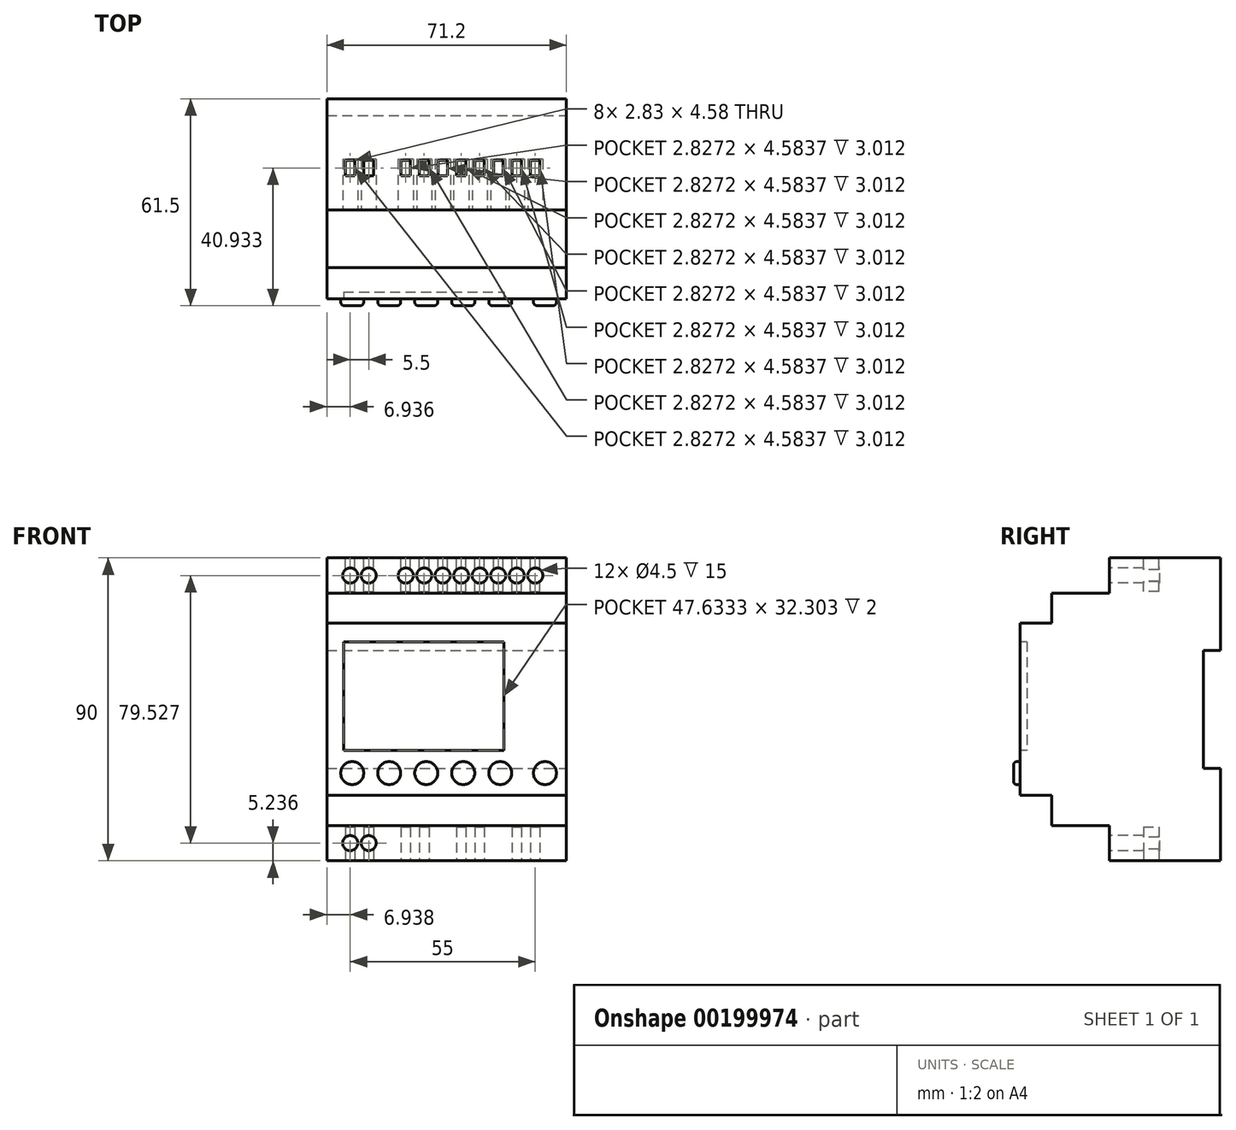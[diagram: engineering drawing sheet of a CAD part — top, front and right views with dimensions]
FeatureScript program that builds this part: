
annotation { "Feature Type Name" : "Feature", "Feature Type Description" : "" }
export const myFeature = defineFeature(function(context is Context, id is Id, definition is map)
    precondition{}
    {
        {
            var Q0;
            Q0=qCreatedBy(makeId("Front.planeOp"),FACE);
            var sketch = newSketch(context, id + "F0", { "sketchPlane" : qUnion([Q0])});
            skLineSegment(sketch, "E0.bottom", {"start": v(35.6, 45) * mm, "end": v(-35.6, 45) * mm});
            skLineSegment(sketch, "E0.top", {"start": v(35.6, -45) * mm, "end": v(-35.6, -45) * mm});
            skLineSegment(sketch, "E0.left", {"start": v(35.6, 45) * mm, "end": v(35.6, -45) * mm});
            skLineSegment(sketch, "E0.right", {"start": v(-35.6, 45) * mm, "end": v(-35.6, -45) * mm});
            skPoint(sketch, "E0.middle", {"position": v(0, 0) * mm});
            skSolve(sketch);
        }
        {
            var Q0;
            Q0=makeQuery(id+"F0.imprint","IMPRINT",FACE,{"disambiguationData":[TD([[makeQuery(id+"F0.imprint","IMPRINT",EDGE,{"derivedFrom":sQuery(id+"F0.wireOp",EDGE,"E0.bottom")}),1.0]])]});
            extrude(context, id + "F1", {"entities" : qUnion([Q0]), "depth" : 59.5 * mm});
        }
        {
            var Q0;
            Q0=makeQuery(id+"F1.opExtrude","SWEPT_FACE",FACE,{"disambiguationData":[OSD([sQuery(id+"F0.wireOp",EDGE,"E0.left")])]});
            var sketch = newSketch(context, id + "F2", { "sketchPlane" : qUnion([Q0])});
            skLineSegment(sketch, "E1.bottom", {"start": v(0, 45) * mm, "end": v(-33, 45) * mm});
            skLineSegment(sketch, "E1.top", {"start": v(0, -45) * mm, "end": v(-33, -45) * mm});
            skLineSegment(sketch, "E1.left", {"start": v(0, 45) * mm, "end": v(0, -45) * mm});
            skLineSegment(sketch, "E1.right", {"start": v(-33, 45) * mm, "end": v(-33, 34.53) * mm});
            skLineSegment(sketch, "E2.bottom", {"start": v(-33, 34.53) * mm, "end": v(-50.17, 34.53) * mm});
            skLineSegment(sketch, "E2.top", {"start": v(-33, -34.53) * mm, "end": v(-50.17, -34.53) * mm});
            skLineSegment(sketch, "E2.right", {"start": v(-50.17, 34.53) * mm, "end": v(-50.17, 25.58) * mm});
            skLineSegment(sketch, "E3.bottom", {"start": v(-50.17, 25.58) * mm, "end": v(-63.34, 25.58) * mm});
            skLineSegment(sketch, "E3.top", {"start": v(-50.17, -25.58) * mm, "end": v(-63.34, -25.58) * mm});
            skLineSegment(sketch, "E4.trimOffspring", {"start": v(-50.17, -25.58) * mm, "end": v(-50.17, -34.53) * mm});
            skLineSegment(sketch, "E5.trimOffspring", {"start": v(-33, -34.53) * mm, "end": v(-33, -45) * mm});
            skLineSegment(sketch, "E6.bottom", {"start": v(5, 17.5) * mm, "end": v(-5, 17.5) * mm});
            skLineSegment(sketch, "E6.top", {"start": v(5, -17.5) * mm, "end": v(-5, -17.5) * mm});
            skLineSegment(sketch, "E6.left", {"start": v(5, 17.5) * mm, "end": v(5, -17.5) * mm});
            skLineSegment(sketch, "E6.right", {"start": v(-5, 17.5) * mm, "end": v(-5, -17.5) * mm});
            skPoint(sketch, "E6.middle", {"position": v(0, 0) * mm});
            skSolve(sketch);
        }
        {
            var Q0;
            {var subQ7=sQuery(id+"F2.wireOp",EDGE,"E1.right");Q0=makeQuery(id+"F2.imprint","IMPRINT",FACE,{"disambiguationData":[TD([[makeQuery(id+"F2.imprint","IMPRINT",EDGE,{"derivedFrom":subQ7}),-1.0]])]});}
            var Q1;
            Q1=makeQuery(id+"F2.imprint","IMPRINT",FACE,{"disambiguationData":[TD([[makeQuery(id+"F2.imprint","IMPRINT",EDGE,{"derivedFrom":sQuery(id+"F2.wireOp",EDGE,"E2.top")}),1.0]])]});
            var Q2;
            {var subQ5=sQuery(id+"F2.wireOp",EDGE,"E6.right");Q2=makeQuery(id+"F2.imprint","IMPRINT",FACE,{"disambiguationData":[TD([[makeQuery(id+"F2.imprint","IMPRINT",EDGE,{"derivedFrom":subQ5}),1.0]])]});}
            extrude(context, id + "F3", {"entities" : qUnion([Q0, Q1, Q2]), "operationType" : NewBodyOperationType.REMOVE, "endBound" : BoundingType.UP_TO_NEXT, "oppositeDirection" : true, "depth" : 25 * mm});
        }
        {
            var Q0;
            Q0=makeQuery(id+"F1.opExtrude","CAP_FACE",FACE,{"disambiguationData":[OSD([sQuery(id+"F0.wireOp",EDGE,"E0.bottom"),sQuery(id+"F0.wireOp",EDGE,"E0.top"),sQuery(id+"F0.wireOp",EDGE,"E0.left"),sQuery(id+"F0.wireOp",EDGE,"E0.right")])],"isStart":false});
            var sketch = newSketch(context, id + "F4", { "sketchPlane" : qUnion([Q0])});
            skLineSegment(sketch, "E7.bottom", {"start": v(-30.62, 20.1) * mm, "end": v(17.02, 20.1) * mm});
            skLineSegment(sketch, "E7.top", {"start": v(-30.62, -12.2) * mm, "end": v(17.02, -12.2) * mm});
            skLineSegment(sketch, "E7.left", {"start": v(-30.62, 20.1) * mm, "end": v(-30.62, -12.2) * mm});
            skLineSegment(sketch, "E7.right", {"start": v(17.02, 20.1) * mm, "end": v(17.02, -12.2) * mm});
            skCircle(sketch, "E8", {"center": v(-28.06, -18.96) * mm, "radius": 3.4 * mm});
            skCircle(sketch, "E9.1.0.0", {"center": v(-17.06, -18.96) * mm, "radius": 3.4 * mm});
            skCircle(sketch, "E9.2.0.0", {"center": v(-6.06, -18.96) * mm, "radius": 3.4 * mm});
            skCircle(sketch, "E9.3.0.0", {"center": v(4.94, -18.96) * mm, "radius": 3.4 * mm});
            skCircle(sketch, "E9.4.0.0", {"center": v(15.94, -18.96) * mm, "radius": 3.4 * mm});
            skLineSegment(sketch, "E9.direction1", {"start": v(-28.06, -18.96) * mm, "end": v(-17.06, -18.96) * mm, "construction": true});
            skCircle(sketch, "E10", {"center": v(29.23, -18.96) * mm, "radius": 3.4 * mm});
            skSolve(sketch);
        }
        {
            var Q0;
            Q0=makeQuery(id+"F4.imprint","IMPRINT",FACE,{"disambiguationData":[TD([[makeQuery(id+"F4.imprint","IMPRINT",EDGE,{"derivedFrom":sQuery(id+"F4.wireOp",EDGE,"E7.bottom")}),-1.0]])]});
            extrude(context, id + "F5", {"entities" : qUnion([Q0]), "operationType" : NewBodyOperationType.REMOVE, "oppositeDirection" : true, "depth" : 2 * mm});
        }
        {
            var Q0;
            Q0=makeQuery(id+"F4.imprint","IMPRINT",FACE,{"disambiguationData":[TD([[makeQuery(id+"F4.imprint","IMPRINT",EDGE,{"derivedFrom":sQuery(id+"F4.wireOp",EDGE,"E8")}),1.0]])]});
            var Q1;
            Q1=makeQuery(id+"F4.imprint","IMPRINT",FACE,{"disambiguationData":[TD([[makeQuery(id+"F4.imprint","IMPRINT",EDGE,{"derivedFrom":sQuery(id+"F4.wireOp",EDGE,"E9.1.0.0")}),1.0]])]});
            var Q2;
            Q2=makeQuery(id+"F4.imprint","IMPRINT",FACE,{"disambiguationData":[TD([[makeQuery(id+"F4.imprint","IMPRINT",EDGE,{"derivedFrom":sQuery(id+"F4.wireOp",EDGE,"E9.2.0.0")}),1.0]])]});
            var Q3;
            Q3=makeQuery(id+"F4.imprint","IMPRINT",FACE,{"disambiguationData":[TD([[makeQuery(id+"F4.imprint","IMPRINT",EDGE,{"derivedFrom":sQuery(id+"F4.wireOp",EDGE,"E9.3.0.0")}),1.0]])]});
            var Q4;
            Q4=makeQuery(id+"F4.imprint","IMPRINT",FACE,{"disambiguationData":[TD([[makeQuery(id+"F4.imprint","IMPRINT",EDGE,{"derivedFrom":sQuery(id+"F4.wireOp",EDGE,"E9.4.0.0")}),1.0]])]});
            var Q5;
            Q5=makeQuery(id+"F4.imprint","IMPRINT",FACE,{"disambiguationData":[TD([[makeQuery(id+"F4.imprint","IMPRINT",EDGE,{"derivedFrom":sQuery(id+"F4.wireOp",EDGE,"E10")}),1.0]])]});
            extrude(context, id + "F6", {"entities" : qUnion([Q0, Q1, Q2, Q3, Q4, Q5]), "operationType" : NewBodyOperationType.ADD, "depth" : 2 * mm});
        }
        {
            var Q0;
            Q0=makeQuery(id+"F6.opExtrude","CAP_FACE",FACE,{"disambiguationData":[OSD([sQuery(id+"F4.wireOp",EDGE,"E8")])],"isStart":false});
            var Q1;
            Q1=makeQuery(id+"F6.opExtrude","CAP_FACE",FACE,{"disambiguationData":[OSD([sQuery(id+"F4.wireOp",EDGE,"E9.1.0.0")])],"isStart":false});
            var Q2;
            Q2=makeQuery(id+"F6.opExtrude","CAP_FACE",FACE,{"disambiguationData":[OSD([sQuery(id+"F4.wireOp",EDGE,"E9.2.0.0")])],"isStart":false});
            var Q3;
            Q3=makeQuery(id+"F6.opExtrude","CAP_FACE",FACE,{"disambiguationData":[OSD([sQuery(id+"F4.wireOp",EDGE,"E9.3.0.0")])],"isStart":false});
            var Q4;
            Q4=makeQuery(id+"F6.opExtrude","CAP_FACE",FACE,{"disambiguationData":[OSD([sQuery(id+"F4.wireOp",EDGE,"E9.4.0.0")])],"isStart":false});
            var Q5;
            Q5=makeQuery(id+"F6.opExtrude","CAP_FACE",FACE,{"disambiguationData":[OSD([sQuery(id+"F4.wireOp",EDGE,"E10")])],"isStart":false});
            fillet(context, id + "F7", {"entities" : qUnion([Q0, Q1, Q2, Q3, Q4, Q5]), "radius" : 1 * mm, "tangentPropagation" : true, "allowEdgeOverflow" : false});
        }
        {
            var Q0;
            Q0=makeQuery(id+"F3.boolean.opBoolean","COPY",FACE,{"derivedFrom":makeQuery(id+"F3.opExtrude","SWEPT_FACE",FACE,{"disambiguationData":[OSD([sQuery(id+"F2.wireOp",EDGE,"E1.right")])]})});
            var sketch = newSketch(context, id + "F8", { "sketchPlane" : qUnion([Q0])});
            skCircle(sketch, "E11", {"center": v(-28.66, 39.76) * mm, "radius": 2.25 * mm});
            skPoint(sketch, "E11.centerSnap0", {"position": v(-35.6, 39.76) * mm});
            skCircle(sketch, "E12.1.0.0", {"center": v(-23.16, 39.76) * mm, "radius": 2.25 * mm});
            skLineSegment(sketch, "E12.direction1", {"start": v(-28.66, 39.76) * mm, "end": v(-23.16, 39.76) * mm, "construction": true});
            skCircle(sketch, "E13.0.3.0", {"center": v(-12.16, 39.76) * mm, "radius": 2.25 * mm});
            skCircle(sketch, "E13.0.4.0", {"center": v(-6.66, 39.76) * mm, "radius": 2.25 * mm});
            skCircle(sketch, "E13.0.5.0", {"center": v(-1.16, 39.76) * mm, "radius": 2.25 * mm});
            skCircle(sketch, "E13.0.6.0", {"center": v(4.34, 39.76) * mm, "radius": 2.25 * mm});
            skCircle(sketch, "E13.0.7.0", {"center": v(9.84, 39.76) * mm, "radius": 2.25 * mm});
            skCircle(sketch, "E13.0.8.0", {"center": v(15.34, 39.76) * mm, "radius": 2.25 * mm});
            skCircle(sketch, "E13.0.9.0", {"center": v(20.84, 39.76) * mm, "radius": 2.25 * mm});
            skCircle(sketch, "E13.0.10.0", {"center": v(26.34, 39.76) * mm, "radius": 2.25 * mm});
            skCircle(sketch, "E14.MirrorC", {"center": v(-23.16, -39.76) * mm, "radius": 2.25 * mm});
            skCircle(sketch, "E15.MirrorC", {"center": v(-28.66, -39.76) * mm, "radius": 2.25 * mm});
            skCircle(sketch, "E16.MirrorC", {"center": v(-6.66, -39.76) * mm, "radius": 2.25 * mm});
            skCircle(sketch, "E17.MirrorC", {"center": v(-12.16, -39.76) * mm, "radius": 2.25 * mm});
            skCircle(sketch, "E18.MirrorC", {"center": v(26.34, -39.76) * mm, "radius": 2.25 * mm});
            skCircle(sketch, "E19.MirrorC", {"center": v(20.84, -39.76) * mm, "radius": 2.25 * mm});
            skCircle(sketch, "E20.MirrorC", {"center": v(9.84, -39.76) * mm, "radius": 2.25 * mm});
            skCircle(sketch, "E21.MirrorC", {"center": v(4.34, -39.76) * mm, "radius": 2.25 * mm});
            skSolve(sketch);
        }
        {
            var Q0;
            Q0=makeQuery(id+"F8.imprint","IMPRINT",FACE,{"disambiguationData":[TD([[makeQuery(id+"F8.imprint","IMPRINT",EDGE,{"derivedFrom":sQuery(id+"F8.wireOp",EDGE,"E11")}),1.0]])]});
            var Q1;
            Q1=makeQuery(id+"F8.imprint","IMPRINT",FACE,{"disambiguationData":[TD([[makeQuery(id+"F8.imprint","IMPRINT",EDGE,{"derivedFrom":sQuery(id+"F8.wireOp",EDGE,"E12.1.0.0")}),1.0]])]});
            var Q2;
            Q2=makeQuery(id+"F8.imprint","IMPRINT",FACE,{"disambiguationData":[TD([[makeQuery(id+"F8.imprint","IMPRINT",EDGE,{"derivedFrom":sQuery(id+"F8.wireOp",EDGE,"E13.0.3.0")}),1.0]])]});
            var Q3;
            Q3=makeQuery(id+"F8.imprint","IMPRINT",FACE,{"disambiguationData":[TD([[makeQuery(id+"F8.imprint","IMPRINT",EDGE,{"derivedFrom":sQuery(id+"F8.wireOp",EDGE,"E13.0.5.0")}),1.0]])]});
            var Q4;
            Q4=makeQuery(id+"F8.imprint","IMPRINT",FACE,{"disambiguationData":[TD([[makeQuery(id+"F8.imprint","IMPRINT",EDGE,{"derivedFrom":sQuery(id+"F8.wireOp",EDGE,"E13.0.6.0")}),1.0]])]});
            var Q5;
            Q5=makeQuery(id+"F8.imprint","IMPRINT",FACE,{"disambiguationData":[TD([[makeQuery(id+"F8.imprint","IMPRINT",EDGE,{"derivedFrom":sQuery(id+"F8.wireOp",EDGE,"E13.0.7.0")}),1.0]])]});
            var Q6;
            Q6=makeQuery(id+"F8.imprint","IMPRINT",FACE,{"disambiguationData":[TD([[makeQuery(id+"F8.imprint","IMPRINT",EDGE,{"derivedFrom":sQuery(id+"F8.wireOp",EDGE,"E13.0.8.0")}),1.0]])]});
            var Q7;
            Q7=makeQuery(id+"F8.imprint","IMPRINT",FACE,{"disambiguationData":[TD([[makeQuery(id+"F8.imprint","IMPRINT",EDGE,{"derivedFrom":sQuery(id+"F8.wireOp",EDGE,"E13.0.9.0")}),1.0]])]});
            var Q8;
            Q8=makeQuery(id+"F8.imprint","IMPRINT",FACE,{"disambiguationData":[TD([[makeQuery(id+"F8.imprint","IMPRINT",EDGE,{"derivedFrom":sQuery(id+"F8.wireOp",EDGE,"E13.0.10.0")}),1.0]])]});
            var Q9;
            Q9=makeQuery(id+"F8.imprint","IMPRINT",FACE,{"disambiguationData":[TD([[makeQuery(id+"F8.imprint","IMPRINT",EDGE,{"derivedFrom":sQuery(id+"F8.wireOp",EDGE,"E15.MirrorC")}),1.0]])]});
            var Q10;
            Q10=makeQuery(id+"F8.imprint","IMPRINT",FACE,{"disambiguationData":[TD([[makeQuery(id+"F8.imprint","IMPRINT",EDGE,{"derivedFrom":sQuery(id+"F8.wireOp",EDGE,"E14.MirrorC")}),1.0]])]});
            var Q11;
            Q11=makeQuery(id+"F8.imprint","IMPRINT",FACE,{"disambiguationData":[TD([[makeQuery(id+"F8.imprint","IMPRINT",EDGE,{"derivedFrom":sQuery(id+"F8.wireOp",EDGE,"E17.MirrorC")}),-1.0]])]});
            var Q12;
            Q12=makeQuery(id+"F8.imprint","IMPRINT",FACE,{"disambiguationData":[TD([[makeQuery(id+"F8.imprint","IMPRINT",EDGE,{"derivedFrom":sQuery(id+"F8.wireOp",EDGE,"E16.MirrorC")}),-1.0]])]});
            var Q13;
            Q13=makeQuery(id+"F8.imprint","IMPRINT",FACE,{"disambiguationData":[TD([[makeQuery(id+"F8.imprint","IMPRINT",EDGE,{"derivedFrom":sQuery(id+"F8.wireOp",EDGE,"E21.MirrorC")}),-1.0]])]});
            var Q14;
            Q14=makeQuery(id+"F8.imprint","IMPRINT",FACE,{"disambiguationData":[TD([[makeQuery(id+"F8.imprint","IMPRINT",EDGE,{"derivedFrom":sQuery(id+"F8.wireOp",EDGE,"E20.MirrorC")}),-1.0]])]});
            var Q15;
            Q15=makeQuery(id+"F8.imprint","IMPRINT",FACE,{"disambiguationData":[TD([[makeQuery(id+"F8.imprint","IMPRINT",EDGE,{"derivedFrom":sQuery(id+"F8.wireOp",EDGE,"E19.MirrorC")}),-1.0]])]});
            var Q16;
            Q16=makeQuery(id+"F8.imprint","IMPRINT",FACE,{"disambiguationData":[TD([[makeQuery(id+"F8.imprint","IMPRINT",EDGE,{"derivedFrom":sQuery(id+"F8.wireOp",EDGE,"E18.MirrorC")}),-1.0]])]});
            var Q17;
            Q17=makeQuery(id+"F8.imprint","IMPRINT",FACE,{"disambiguationData":[TD([[makeQuery(id+"F8.imprint","IMPRINT",EDGE,{"derivedFrom":sQuery(id+"F8.wireOp",EDGE,"E13.0.3.0")}),1.0]])]});
            var Q18;
            Q18=makeQuery(id+"F8.imprint","IMPRINT",FACE,{"disambiguationData":[TD([[makeQuery(id+"F8.imprint","IMPRINT",EDGE,{"derivedFrom":sQuery(id+"F8.wireOp",EDGE,"E12.1.0.0")}),-1.0]])]});
            var Q19;
            Q19=makeQuery(id+"F8.imprint","IMPRINT",FACE,{"disambiguationData":[TD([[makeQuery(id+"F8.imprint","IMPRINT",EDGE,{"derivedFrom":sQuery(id+"F8.wireOp",EDGE,"E11")}),-1.0]])]});
            var Q20;
            Q20=makeQuery(id+"F8.imprint","IMPRINT",FACE,{"disambiguationData":[TD([[makeQuery(id+"F8.imprint","IMPRINT",EDGE,{"derivedFrom":sQuery(id+"F8.wireOp",EDGE,"E13.0.4.0")}),1.0]])]});
            extrude(context, id + "F9", {"entities" : qUnion([Q0, Q1, Q2, Q3, Q4, Q5, Q6, Q7, Q8, Q9, Q10, Q11, Q12, Q13, Q14, Q15, Q16, Q17, Q18, Q19, Q20]), "operationType" : NewBodyOperationType.REMOVE, "oppositeDirection" : true, "depth" : 15 * mm});
        }
        {
            var Q0;
            Q0=makeQuery(id+"F1.opExtrude","SWEPT_FACE",FACE,{"disambiguationData":[OSD([sQuery(id+"F0.wireOp",EDGE,"E0.bottom")])]});
            var sketch = newSketch(context, id + "F10", { "sketchPlane" : qUnion([Q0])});
            skLineSegment(sketch, "E22.left", {"start": v(-27.25, -18.27) * mm, "end": v(-27.25, -22.86) * mm});
            skLineSegment(sketch, "E22.right", {"start": v(-30.08, -18.27) * mm, "end": v(-30.08, -22.86) * mm});
            skLineSegment(sketch, "E23", {"start": v(-30.08, -22.86) * mm, "end": v(-27.25, -22.86) * mm});
            skLineSegment(sketch, "E24", {"start": v(-30.08, -18.27) * mm, "end": v(-27.25, -18.27) * mm});
            skLineSegment(sketch, "E25.1.0.0", {"start": v(-24.58, -18.27) * mm, "end": v(-24.58, -22.86) * mm});
            skLineSegment(sketch, "E25.1.0.1", {"start": v(-24.58, -18.27) * mm, "end": v(-21.75, -18.27) * mm});
            skLineSegment(sketch, "E25.1.0.2", {"start": v(-24.58, -22.86) * mm, "end": v(-21.75, -22.86) * mm});
            skLineSegment(sketch, "E25.1.0.3", {"start": v(-21.75, -18.27) * mm, "end": v(-21.75, -22.86) * mm});
            skLineSegment(sketch, "E25.3.0.0", {"start": v(-13.58, -18.27) * mm, "end": v(-13.58, -22.86) * mm});
            skLineSegment(sketch, "E25.3.0.1", {"start": v(-13.58, -18.27) * mm, "end": v(-10.75, -18.27) * mm});
            skLineSegment(sketch, "E25.3.0.2", {"start": v(-13.58, -22.86) * mm, "end": v(-10.75, -22.86) * mm});
            skLineSegment(sketch, "E25.3.0.3", {"start": v(-10.75, -18.27) * mm, "end": v(-10.75, -22.86) * mm});
            skLineSegment(sketch, "E25.4.0.0", {"start": v(-8.08, -18.27) * mm, "end": v(-8.08, -22.86) * mm});
            skLineSegment(sketch, "E25.4.0.1", {"start": v(-8.08, -18.27) * mm, "end": v(-5.25, -18.27) * mm});
            skLineSegment(sketch, "E25.4.0.2", {"start": v(-8.08, -22.86) * mm, "end": v(-5.25, -22.86) * mm});
            skLineSegment(sketch, "E25.4.0.3", {"start": v(-5.25, -18.27) * mm, "end": v(-5.25, -22.86) * mm});
            skLineSegment(sketch, "E25.5.0.0", {"start": v(-2.58, -18.27) * mm, "end": v(-2.58, -22.86) * mm});
            skLineSegment(sketch, "E25.5.0.1", {"start": v(-2.58, -18.27) * mm, "end": v(0.25, -18.27) * mm});
            skLineSegment(sketch, "E25.5.0.2", {"start": v(-2.58, -22.86) * mm, "end": v(0.25, -22.86) * mm});
            skLineSegment(sketch, "E25.5.0.3", {"start": v(0.25, -18.27) * mm, "end": v(0.25, -22.86) * mm});
            skLineSegment(sketch, "E25.6.0.0", {"start": v(2.92, -18.27) * mm, "end": v(2.92, -22.86) * mm});
            skLineSegment(sketch, "E25.6.0.1", {"start": v(2.92, -18.27) * mm, "end": v(5.75, -18.27) * mm});
            skLineSegment(sketch, "E25.6.0.2", {"start": v(2.92, -22.86) * mm, "end": v(5.75, -22.86) * mm});
            skLineSegment(sketch, "E25.6.0.3", {"start": v(5.75, -18.27) * mm, "end": v(5.75, -22.86) * mm});
            skLineSegment(sketch, "E25.7.0.0", {"start": v(8.42, -18.27) * mm, "end": v(8.42, -22.86) * mm});
            skLineSegment(sketch, "E25.7.0.1", {"start": v(8.42, -18.27) * mm, "end": v(11.25, -18.27) * mm});
            skLineSegment(sketch, "E25.7.0.2", {"start": v(8.42, -22.86) * mm, "end": v(11.25, -22.86) * mm});
            skLineSegment(sketch, "E25.7.0.3", {"start": v(11.25, -18.27) * mm, "end": v(11.25, -22.86) * mm});
            skLineSegment(sketch, "E25.8.0.0", {"start": v(13.92, -18.27) * mm, "end": v(13.92, -22.86) * mm});
            skLineSegment(sketch, "E25.8.0.1", {"start": v(13.92, -18.27) * mm, "end": v(16.75, -18.27) * mm});
            skLineSegment(sketch, "E25.8.0.2", {"start": v(13.92, -22.86) * mm, "end": v(16.75, -22.86) * mm});
            skLineSegment(sketch, "E25.8.0.3", {"start": v(16.75, -18.27) * mm, "end": v(16.75, -22.86) * mm});
            skLineSegment(sketch, "E25.9.0.0", {"start": v(19.42, -18.27) * mm, "end": v(19.42, -22.86) * mm});
            skLineSegment(sketch, "E25.9.0.1", {"start": v(19.42, -18.27) * mm, "end": v(22.25, -18.27) * mm});
            skLineSegment(sketch, "E25.9.0.2", {"start": v(19.42, -22.86) * mm, "end": v(22.25, -22.86) * mm});
            skLineSegment(sketch, "E25.9.0.3", {"start": v(22.25, -18.27) * mm, "end": v(22.25, -22.86) * mm});
            skLineSegment(sketch, "E25.10.0.0", {"start": v(24.92, -18.27) * mm, "end": v(24.92, -22.86) * mm});
            skLineSegment(sketch, "E25.10.0.1", {"start": v(24.92, -18.27) * mm, "end": v(27.75, -18.27) * mm});
            skLineSegment(sketch, "E25.10.0.2", {"start": v(24.92, -22.86) * mm, "end": v(27.75, -22.86) * mm});
            skLineSegment(sketch, "E25.10.0.3", {"start": v(27.75, -18.27) * mm, "end": v(27.75, -22.86) * mm});
            skLineSegment(sketch, "E25.direction1", {"start": v(-30.08, -22.86) * mm, "end": v(-24.58, -22.86) * mm, "construction": true});
            skSolve(sketch);
        }
        {
            var Q0;
            Q0=makeQuery(id+"F10.imprint","IMPRINT",FACE,{"disambiguationData":[TD([[makeQuery(id+"F10.imprint","IMPRINT",EDGE,{"derivedFrom":sQuery(id+"F10.wireOp",EDGE,"E22.left")}),-1.0]])]});
            var Q1;
            Q1=makeQuery(id+"F10.imprint","IMPRINT",FACE,{"disambiguationData":[TD([[makeQuery(id+"F10.imprint","IMPRINT",EDGE,{"derivedFrom":sQuery(id+"F10.wireOp",EDGE,"E25.1.0.0")}),1.0]])]});
            var Q2;
            Q2=makeQuery(id+"F10.imprint","IMPRINT",FACE,{"disambiguationData":[TD([[makeQuery(id+"F10.imprint","IMPRINT",EDGE,{"derivedFrom":sQuery(id+"F10.wireOp",EDGE,"E25.3.0.0")}),1.0]])]});
            var Q3;
            Q3=makeQuery(id+"F10.imprint","IMPRINT",FACE,{"disambiguationData":[TD([[makeQuery(id+"F10.imprint","IMPRINT",EDGE,{"derivedFrom":sQuery(id+"F10.wireOp",EDGE,"E25.4.0.0")}),1.0]])]});
            var Q4;
            Q4=makeQuery(id+"F10.imprint","IMPRINT",FACE,{"disambiguationData":[TD([[makeQuery(id+"F10.imprint","IMPRINT",EDGE,{"derivedFrom":sQuery(id+"F10.wireOp",EDGE,"E25.5.0.0")}),1.0]])]});
            var Q5;
            Q5=makeQuery(id+"F10.imprint","IMPRINT",FACE,{"disambiguationData":[TD([[makeQuery(id+"F10.imprint","IMPRINT",EDGE,{"derivedFrom":sQuery(id+"F10.wireOp",EDGE,"E25.6.0.0")}),1.0]])]});
            var Q6;
            Q6=makeQuery(id+"F10.imprint","IMPRINT",FACE,{"disambiguationData":[TD([[makeQuery(id+"F10.imprint","IMPRINT",EDGE,{"derivedFrom":sQuery(id+"F10.wireOp",EDGE,"E25.7.0.0")}),1.0]])]});
            var Q7;
            Q7=makeQuery(id+"F10.imprint","IMPRINT",FACE,{"disambiguationData":[TD([[makeQuery(id+"F10.imprint","IMPRINT",EDGE,{"derivedFrom":sQuery(id+"F10.wireOp",EDGE,"E25.8.0.0")}),1.0]])]});
            var Q8;
            Q8=makeQuery(id+"F10.imprint","IMPRINT",FACE,{"disambiguationData":[TD([[makeQuery(id+"F10.imprint","IMPRINT",EDGE,{"derivedFrom":sQuery(id+"F10.wireOp",EDGE,"E25.9.0.0")}),1.0]])]});
            var Q9;
            Q9=makeQuery(id+"F10.imprint","IMPRINT",FACE,{"disambiguationData":[TD([[makeQuery(id+"F10.imprint","IMPRINT",EDGE,{"derivedFrom":sQuery(id+"F10.wireOp",EDGE,"E25.10.0.0")}),1.0]])]});
            extrude(context, id + "F11", {"entities" : qUnion([Q0, Q1, Q2, Q3, Q4, Q5, Q6, Q7, Q8, Q9]), "operationType" : NewBodyOperationType.REMOVE, "oppositeDirection" : true, "depth" : 10 * mm});
        }
        {
            var Q0;
            Q0=makeQuery(id+"F1.opExtrude","SWEPT_FACE",FACE,{"disambiguationData":[OSD([sQuery(id+"F0.wireOp",EDGE,"E0.top")])]});
            var sketch = newSketch(context, id + "F12", { "sketchPlane" : qUnion([Q0])});
            skLineSegment(sketch, "E26.bottom", {"start": v(-30.08, 22.86) * mm, "end": v(-27.25, 22.86) * mm});
            skLineSegment(sketch, "E26.top", {"start": v(-30.08, 18.27) * mm, "end": v(-27.25, 18.27) * mm});
            skLineSegment(sketch, "E26.left", {"start": v(-30.08, 22.86) * mm, "end": v(-30.08, 18.27) * mm});
            skLineSegment(sketch, "E26.right", {"start": v(-27.25, 22.86) * mm, "end": v(-27.25, 18.27) * mm});
            skLineSegment(sketch, "E27.bottom", {"start": v(-24.58, 22.86) * mm, "end": v(-21.75, 22.86) * mm});
            skLineSegment(sketch, "E27.top", {"start": v(-24.58, 18.27) * mm, "end": v(-21.75, 18.27) * mm});
            skLineSegment(sketch, "E27.left", {"start": v(-24.58, 22.86) * mm, "end": v(-24.58, 18.27) * mm});
            skLineSegment(sketch, "E27.right", {"start": v(-21.75, 22.86) * mm, "end": v(-21.75, 18.27) * mm});
            skLineSegment(sketch, "E28.bottom", {"start": v(-13.58, 22.86) * mm, "end": v(-10.75, 22.86) * mm});
            skLineSegment(sketch, "E28.top", {"start": v(-13.58, 18.27) * mm, "end": v(-10.75, 18.27) * mm});
            skLineSegment(sketch, "E28.left", {"start": v(-13.58, 22.86) * mm, "end": v(-13.58, 18.27) * mm});
            skLineSegment(sketch, "E28.right", {"start": v(-10.75, 22.86) * mm, "end": v(-10.75, 18.27) * mm});
            skLineSegment(sketch, "E29.bottom", {"start": v(-8.08, 22.86) * mm, "end": v(-5.25, 22.86) * mm});
            skLineSegment(sketch, "E29.top", {"start": v(-8.08, 18.27) * mm, "end": v(-5.25, 18.27) * mm});
            skLineSegment(sketch, "E29.left", {"start": v(-8.08, 22.86) * mm, "end": v(-8.08, 18.27) * mm});
            skLineSegment(sketch, "E29.right", {"start": v(-5.25, 22.86) * mm, "end": v(-5.25, 18.27) * mm});
            skLineSegment(sketch, "E30.bottom", {"start": v(2.92, 22.86) * mm, "end": v(5.75, 22.86) * mm});
            skLineSegment(sketch, "E30.top", {"start": v(2.92, 18.27) * mm, "end": v(5.75, 18.27) * mm});
            skLineSegment(sketch, "E30.left", {"start": v(2.92, 22.86) * mm, "end": v(2.92, 18.27) * mm});
            skLineSegment(sketch, "E30.right", {"start": v(5.75, 22.86) * mm, "end": v(5.75, 18.27) * mm});
            skLineSegment(sketch, "E31.bottom", {"start": v(8.42, 22.86) * mm, "end": v(11.25, 22.86) * mm});
            skLineSegment(sketch, "E31.top", {"start": v(8.42, 18.27) * mm, "end": v(11.25, 18.27) * mm});
            skLineSegment(sketch, "E31.left", {"start": v(8.42, 22.86) * mm, "end": v(8.42, 18.27) * mm});
            skLineSegment(sketch, "E31.right", {"start": v(11.25, 22.86) * mm, "end": v(11.25, 18.27) * mm});
            skLineSegment(sketch, "E32.bottom", {"start": v(19.42, 22.86) * mm, "end": v(22.25, 22.86) * mm});
            skLineSegment(sketch, "E32.top", {"start": v(19.42, 18.27) * mm, "end": v(22.25, 18.27) * mm});
            skLineSegment(sketch, "E32.left", {"start": v(19.42, 22.86) * mm, "end": v(19.42, 18.27) * mm});
            skLineSegment(sketch, "E32.right", {"start": v(22.25, 22.86) * mm, "end": v(22.25, 18.27) * mm});
            skLineSegment(sketch, "E33.bottom", {"start": v(24.92, 22.86) * mm, "end": v(27.75, 22.86) * mm});
            skLineSegment(sketch, "E33.top", {"start": v(24.92, 18.27) * mm, "end": v(27.75, 18.27) * mm});
            skLineSegment(sketch, "E33.left", {"start": v(24.92, 22.86) * mm, "end": v(24.92, 18.27) * mm});
            skLineSegment(sketch, "E33.right", {"start": v(27.75, 22.86) * mm, "end": v(27.75, 18.27) * mm});
            skSolve(sketch);
        }
        {
            var Q0;
            Q0=makeQuery(id+"F12.imprint","IMPRINT",FACE,{"disambiguationData":[TD([[makeQuery(id+"F12.imprint","IMPRINT",EDGE,{"derivedFrom":sQuery(id+"F12.wireOp",EDGE,"E26.bottom")}),-1.0]])]});
            var Q1;
            Q1=makeQuery(id+"F12.imprint","IMPRINT",FACE,{"disambiguationData":[TD([[makeQuery(id+"F12.imprint","IMPRINT",EDGE,{"derivedFrom":sQuery(id+"F12.wireOp",EDGE,"E27.bottom")}),-1.0]])]});
            var Q2;
            Q2=makeQuery(id+"F12.imprint","IMPRINT",FACE,{"disambiguationData":[TD([[makeQuery(id+"F12.imprint","IMPRINT",EDGE,{"derivedFrom":sQuery(id+"F12.wireOp",EDGE,"E28.bottom")}),-1.0]])]});
            var Q3;
            Q3=makeQuery(id+"F12.imprint","IMPRINT",FACE,{"disambiguationData":[TD([[makeQuery(id+"F12.imprint","IMPRINT",EDGE,{"derivedFrom":sQuery(id+"F12.wireOp",EDGE,"E29.bottom")}),-1.0]])]});
            var Q4;
            Q4=makeQuery(id+"F12.imprint","IMPRINT",FACE,{"disambiguationData":[TD([[makeQuery(id+"F12.imprint","IMPRINT",EDGE,{"derivedFrom":sQuery(id+"F12.wireOp",EDGE,"E30.bottom")}),-1.0]])]});
            var Q5;
            Q5=makeQuery(id+"F12.imprint","IMPRINT",FACE,{"disambiguationData":[TD([[makeQuery(id+"F12.imprint","IMPRINT",EDGE,{"derivedFrom":sQuery(id+"F12.wireOp",EDGE,"E31.bottom")}),-1.0]])]});
            var Q6;
            Q6=makeQuery(id+"F12.imprint","IMPRINT",FACE,{"disambiguationData":[TD([[makeQuery(id+"F12.imprint","IMPRINT",EDGE,{"derivedFrom":sQuery(id+"F12.wireOp",EDGE,"E32.bottom")}),-1.0]])]});
            var Q7;
            Q7=makeQuery(id+"F12.imprint","IMPRINT",FACE,{"disambiguationData":[TD([[makeQuery(id+"F12.imprint","IMPRINT",EDGE,{"derivedFrom":sQuery(id+"F12.wireOp",EDGE,"E33.bottom")}),-1.0]])]});
            extrude(context, id + "F13", {"entities" : qUnion([Q0, Q1, Q2, Q3, Q4, Q5, Q6, Q7]), "operationType" : NewBodyOperationType.REMOVE, "oppositeDirection" : true, "depth" : 10 * mm});
        }
    });
